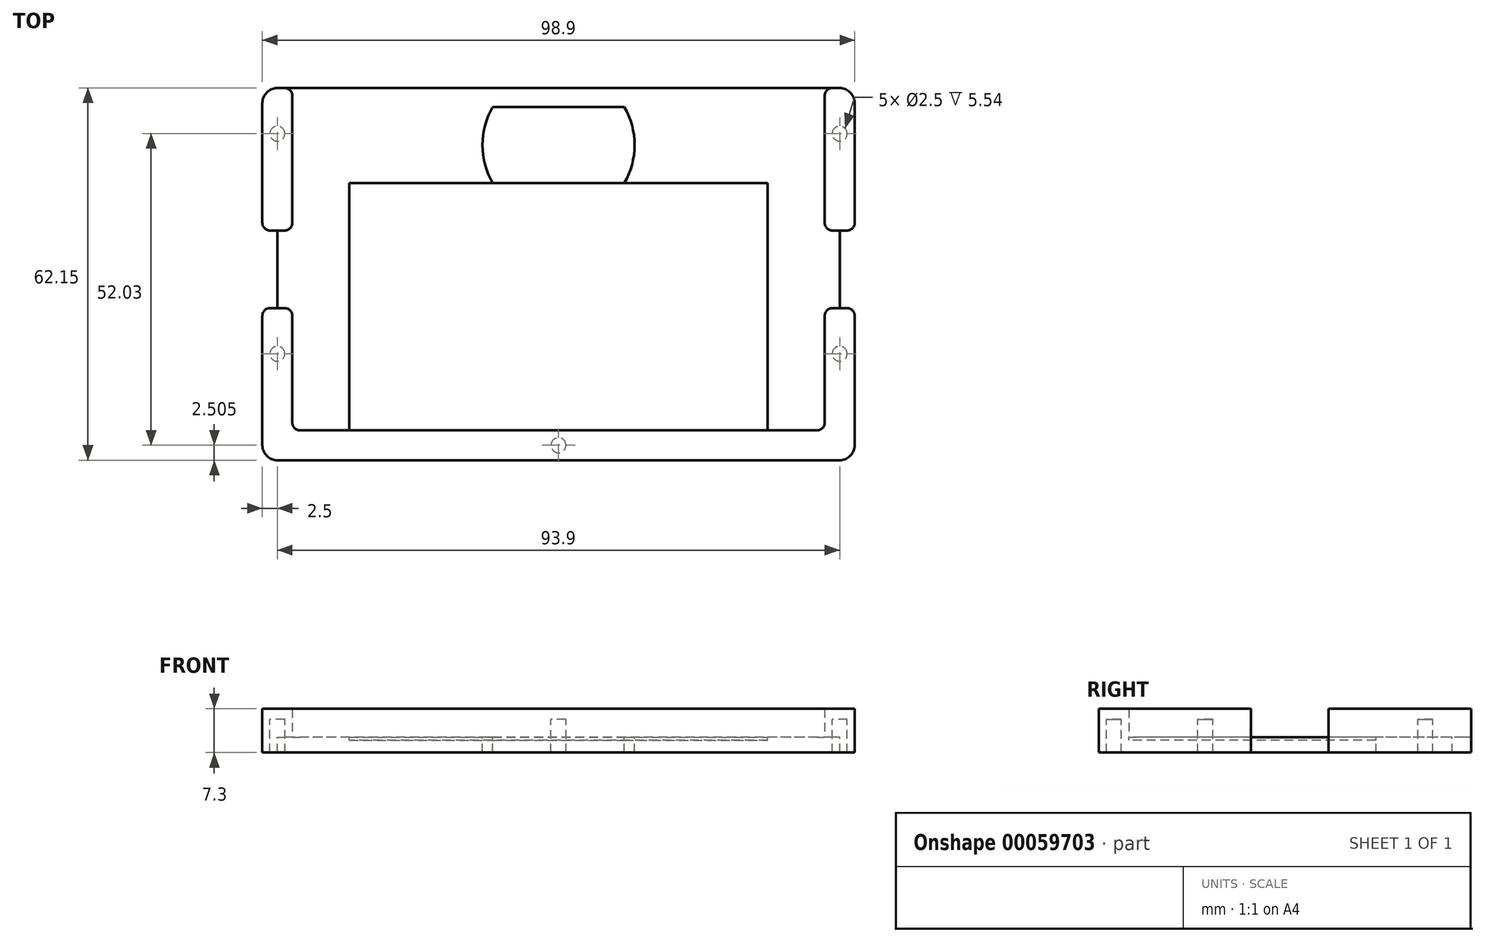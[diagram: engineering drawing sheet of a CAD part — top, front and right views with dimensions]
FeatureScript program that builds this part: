
annotation { "Feature Type Name" : "Feature", "Feature Type Description" : "" }
export const myFeature = defineFeature(function(context is Context, id is Id, definition is map)
    precondition{}
    {
        {
            var Q0;
            Q0=qCreatedBy(makeId("Top.planeOp"),FACE);
            var sketch = newSketch(context, id + "F0", { "sketchPlane" : qUnion([Q0])});
            skLineSegment(sketch, "E0.bottom", {"start": v(44.45, 28.58) * mm, "end": v(-44.45, 28.58) * mm});
            skLineSegment(sketch, "E0.top", {"start": v(44.45, -28.58) * mm, "end": v(-44.45, -28.58) * mm});
            skLineSegment(sketch, "E0.left", {"start": v(44.45, 28.58) * mm, "end": v(44.45, -28.58) * mm});
            skLineSegment(sketch, "E0.right", {"start": v(-44.45, 28.58) * mm, "end": v(-44.45, -28.58) * mm});
            skPoint(sketch, "E0.middle", {"position": v(0, 0) * mm});
            skLineSegment(sketch, "E1", {"start": v(-44.45, 28.58) * mm, "end": v(-49.45, 28.58) * mm});
            skLineSegment(sketch, "E2", {"start": v(-49.45, 28.57) * mm, "end": v(-49.45, -33.58) * mm});
            skLineSegment(sketch, "E3", {"start": v(-49.45, -33.58) * mm, "end": v(49.45, -33.57) * mm});
            skLineSegment(sketch, "E4", {"start": v(49.45, -33.57) * mm, "end": v(49.45, 28.57) * mm});
            skLineSegment(sketch, "E5", {"start": v(49.45, 28.58) * mm, "end": v(44.45, 28.58) * mm});
            skLineSegment(sketch, "E6", {"start": v(0, 0) * mm, "end": v(0, 46.56) * mm, "construction": true});
            skCircle(sketch, "E7", {"center": v(-46.95, 20.95) * mm, "radius": 1.25 * mm});
            skCircle(sketch, "E8", {"center": v(-46.95, -15.8) * mm, "radius": 1.25 * mm});
            skCircle(sketch, "E9", {"center": v(0, -31.08) * mm, "radius": 1.25 * mm});
            skCircle(sketch, "E10", {"center": v(46.95, -15.8) * mm, "radius": 1.25 * mm});
            skCircle(sketch, "E11", {"center": v(46.95, 20.95) * mm, "radius": 1.25 * mm});
            skLineSegment(sketch, "E12", {"start": v(-49.45, 4.78) * mm, "end": v(-44.45, 4.78) * mm});
            skLineSegment(sketch, "E13", {"start": v(-49.45, -8.18) * mm, "end": v(-44.45, -8.18) * mm});
            skLineSegment(sketch, "E14.MirrorCS", {"start": v(49.45, 4.78) * mm, "end": v(44.45, 4.78) * mm});
            skLineSegment(sketch, "E15.MirrorCS", {"start": v(49.45, -8.18) * mm, "end": v(44.45, -8.18) * mm});
            skLineSegment(sketch, "E16", {"start": v(-46.95, 4.78) * mm, "end": v(-46.95, -8.18) * mm});
            skLineSegment(sketch, "E17", {"start": v(46.95, 4.78) * mm, "end": v(46.95, -8.18) * mm});
            skLineSegment(sketch, "E18", {"start": v(-34.92, -28.58) * mm, "end": v(-34.93, 12.7) * mm});
            skLineSegment(sketch, "E19", {"start": v(-34.93, 12.7) * mm, "end": v(34.93, 12.7) * mm});
            skLineSegment(sketch, "E20", {"start": v(34.92, 12.7) * mm, "end": v(34.93, -28.58) * mm});
            skSolve(sketch);
        }
        {
            var Q0;
            Q0=makeQuery(id+"F0.imprint","IMPRINT",FACE,{"disambiguationData":[TD([[makeQuery(id+"F0.imprint","IMPRINT",EDGE,{"derivedFrom":sQuery(id+"F0.wireOp",EDGE,"E0.bottom")}),1.0]])]});
            var Q1;
            {var subQ1=sQuery(id+"F0.wireOp",EDGE,"E1");Q1=makeQuery(id+"F0.imprint","IMPRINT",FACE,{"disambiguationData":[TD([[makeQuery(id+"F0.imprint","IMPRINT",EDGE,{"derivedFrom":subQ1}),1.0]])]});}
            var Q2;
            {var subQ4=sQuery(id+"F0.wireOp",EDGE,"E0.top");Q2=makeQuery(id+"F0.imprint","IMPRINT",FACE,{"disambiguationData":[TD([[makeQuery(id+"F0.imprint","IMPRINT",EDGE,{"derivedFrom":subQ4}),1.0]])]});}
            var Q3;
            {var subQ5=sQuery(id+"F0.wireOp",EDGE,"E16");Q3=makeQuery(id+"F0.imprint","IMPRINT",FACE,{"disambiguationData":[TD([[makeQuery(id+"F0.imprint","IMPRINT",EDGE,{"derivedFrom":subQ5}),1.0]])]});}
            var Q4;
            {var subQ5=sQuery(id+"F0.wireOp",EDGE,"E17");Q4=makeQuery(id+"F0.imprint","IMPRINT",FACE,{"disambiguationData":[TD([[makeQuery(id+"F0.imprint","IMPRINT",EDGE,{"derivedFrom":subQ5}),-1.0]])]});}
            var Q5;
            {var subQ0=sQuery(id+"F0.wireOp",EDGE,"E5");Q5=makeQuery(id+"F0.imprint","IMPRINT",FACE,{"disambiguationData":[TD([[makeQuery(id+"F0.imprint","IMPRINT",EDGE,{"derivedFrom":subQ0}),1.0]])]});}
            var Q6;
            {var subQ0=sQuery(id+"F0.wireOp",EDGE,"E18");Q6=makeQuery(id+"F0.imprint","IMPRINT",FACE,{"disambiguationData":[TD([[makeQuery(id+"F0.imprint","IMPRINT",EDGE,{"derivedFrom":subQ0}),-1.0]])]});}
            extrude(context, id + "F1", {"entities" : qUnion([Q0, Q1, Q2, Q3, Q4, Q5, Q6]), "oppositeDirection" : true, "depth" : 2.54 * mm});
        }
        {
            var Q0;
            {var subQ1=sQuery(id+"F0.wireOp",EDGE,"E1");Q0=makeQuery(id+"F0.imprint","IMPRINT",FACE,{"disambiguationData":[TD([[makeQuery(id+"F0.imprint","IMPRINT",EDGE,{"derivedFrom":subQ1}),1.0]])]});}
            var Q1;
            {var subQ0=sQuery(id+"F0.wireOp",EDGE,"E5");Q1=makeQuery(id+"F0.imprint","IMPRINT",FACE,{"disambiguationData":[TD([[makeQuery(id+"F0.imprint","IMPRINT",EDGE,{"derivedFrom":subQ0}),1.0]])]});}
            var Q2;
            Q2=makeQuery(id+"F0.imprint","IMPRINT",FACE,{"disambiguationData":[TD([[makeQuery(id+"F0.imprint","IMPRINT",EDGE,{"derivedFrom":sQuery(id+"F0.wireOp",EDGE,"E8")}),1.0]])]});
            var Q3;
            Q3=makeQuery(id+"F0.imprint","IMPRINT",FACE,{"disambiguationData":[TD([[makeQuery(id+"F0.imprint","IMPRINT",EDGE,{"derivedFrom":sQuery(id+"F0.wireOp",EDGE,"E7")}),1.0]])]});
            var Q4;
            Q4=makeQuery(id+"F0.imprint","IMPRINT",FACE,{"disambiguationData":[TD([[makeQuery(id+"F0.imprint","IMPRINT",EDGE,{"derivedFrom":sQuery(id+"F0.wireOp",EDGE,"E11")}),1.0]])]});
            var Q5;
            {var subQ4=sQuery(id+"F0.wireOp",EDGE,"E0.top");Q5=makeQuery(id+"F0.imprint","IMPRINT",FACE,{"disambiguationData":[TD([[makeQuery(id+"F0.imprint","IMPRINT",EDGE,{"derivedFrom":subQ4}),1.0]])]});}
            var Q6;
            Q6=makeQuery(id+"F0.imprint","IMPRINT",FACE,{"disambiguationData":[TD([[makeQuery(id+"F0.imprint","IMPRINT",EDGE,{"derivedFrom":sQuery(id+"F0.wireOp",EDGE,"E9")}),1.0]])]});
            var Q7;
            Q7=makeQuery(id+"F0.imprint","IMPRINT",FACE,{"disambiguationData":[TD([[makeQuery(id+"F0.imprint","IMPRINT",EDGE,{"derivedFrom":sQuery(id+"F0.wireOp",EDGE,"E10")}),1.0]])]});
            extrude(context, id + "F2", {"entities" : qUnion([Q0, Q1, Q2, Q3, Q4, Q5, Q6, Q7]), "depth" : 4.76 * mm});
        }
        {
            var Q0;
            {var subQ0=sQuery(id+"F0.wireOp",EDGE,"E18");Q0=makeQuery(id+"F0.imprint","IMPRINT",FACE,{"disambiguationData":[TD([[makeQuery(id+"F0.imprint","IMPRINT",EDGE,{"derivedFrom":subQ0}),-1.0]])]});}
            var Q1;
            {var subQ1=sQuery(id+"F0.wireOp",EDGE,"E3");Q1=makeQuery(id+"F0.imprint","IMPRINT",FACE,{"disambiguationData":[TD([[makeQuery(id+"F0.imprint","IMPRINT",EDGE,{"derivedFrom":subQ1}),1.0]])]});}
            var Q2;
            {var subQ0=sQuery(id+"F0.wireOp",EDGE,"E5");Q2=makeQuery(id+"F0.imprint","IMPRINT",FACE,{"disambiguationData":[TD([[makeQuery(id+"F0.imprint","IMPRINT",EDGE,{"derivedFrom":subQ0}),1.0]])]});}
            var Q3;
            {var subQ1=sQuery(id+"F0.wireOp",EDGE,"E1");Q3=makeQuery(id+"F0.imprint","IMPRINT",FACE,{"disambiguationData":[TD([[makeQuery(id+"F0.imprint","IMPRINT",EDGE,{"derivedFrom":subQ1}),1.0]])]});}
            extrude(context, id + "F3", {"entities" : qUnion([Q0, Q1, Q2, Q3]), "operationType" : NewBodyOperationType.REMOVE, "oppositeDirection" : true, "depth" : 0.5 * mm});
        }
        {
            var Q0;
            Q0=makeQuery(id+"F2.opExtrude","CAP_FACE",FACE,{"disambiguationData":[OSD([sQuery(id+"F0.wireOp",EDGE,"E0.top"),sQuery(id+"F0.wireOp",EDGE,"E0.left"),sQuery(id+"F0.wireOp",EDGE,"E0.right"),sQuery(id+"F0.wireOp",EDGE,"E2"),sQuery(id+"F0.wireOp",EDGE,"E3"),sQuery(id+"F0.wireOp",EDGE,"E4"),sQuery(id+"F0.wireOp",EDGE,"E13"),sQuery(id+"F0.wireOp",EDGE,"E15.MirrorCS")])],"isStart":true});
            var Q1;
            Q1=makeQuery(id+"F2.opExtrude","CAP_FACE",FACE,{"disambiguationData":[OSD([sQuery(id+"F0.wireOp",EDGE,"E0.left"),sQuery(id+"F0.wireOp",EDGE,"E4"),sQuery(id+"F0.wireOp",EDGE,"E5"),sQuery(id+"F0.wireOp",EDGE,"E14.MirrorCS")])],"isStart":true});
            var Q2;
            Q2=makeQuery(id+"F2.opExtrude","CAP_FACE",FACE,{"disambiguationData":[OSD([sQuery(id+"F0.wireOp",EDGE,"E0.right"),sQuery(id+"F0.wireOp",EDGE,"E1"),sQuery(id+"F0.wireOp",EDGE,"E2"),sQuery(id+"F0.wireOp",EDGE,"E12")])],"isStart":true});
            extrude(context, id + "F4", {"entities" : qUnion([Q0, Q1, Q2]), "operationType" : NewBodyOperationType.ADD, "depth" : 0.5 * mm});
        }
        {
            var Q0;
            Q0=makeQuery(id+"F0.imprint","IMPRINT",FACE,{"disambiguationData":[TD([[makeQuery(id+"F0.imprint","IMPRINT",EDGE,{"derivedFrom":sQuery(id+"F0.wireOp",EDGE,"E8")}),1.0]])]});
            var Q1;
            Q1=makeQuery(id+"F0.imprint","IMPRINT",FACE,{"disambiguationData":[TD([[makeQuery(id+"F0.imprint","IMPRINT",EDGE,{"derivedFrom":sQuery(id+"F0.wireOp",EDGE,"E9")}),1.0]])]});
            var Q2;
            Q2=makeQuery(id+"F0.imprint","IMPRINT",FACE,{"disambiguationData":[TD([[makeQuery(id+"F0.imprint","IMPRINT",EDGE,{"derivedFrom":sQuery(id+"F0.wireOp",EDGE,"E10")}),1.0]])]});
            var Q3;
            Q3=makeQuery(id+"F0.imprint","IMPRINT",FACE,{"disambiguationData":[TD([[makeQuery(id+"F0.imprint","IMPRINT",EDGE,{"derivedFrom":sQuery(id+"F0.wireOp",EDGE,"E11")}),1.0]])]});
            var Q4;
            Q4=makeQuery(id+"F0.imprint","IMPRINT",FACE,{"disambiguationData":[TD([[makeQuery(id+"F0.imprint","IMPRINT",EDGE,{"derivedFrom":sQuery(id+"F0.wireOp",EDGE,"E7")}),1.0]])]});
            extrude(context, id + "F5", {"entities" : qUnion([Q0, Q1, Q2, Q3, Q4]), "operationType" : NewBodyOperationType.REMOVE, "endBound" : BoundingType.SYMMETRIC, "depth" : 6 * mm});
        }
        {
            var Q0;
            Q0=makeQuery(id+"F2.opExtrude","SWEPT_EDGE",EDGE,{"disambiguationData":[OSD([sQuery(id+"F0.wireOp",EDGE,"E2"),sQuery(id+"F0.wireOp",EDGE,"E3")])]});
            var Q1;
            Q1=makeQuery(id+"F1.opExtrude","SWEPT_EDGE",EDGE,{"disambiguationData":[OSD([sQuery(id+"F0.wireOp",EDGE,"E2"),sQuery(id+"F0.wireOp",EDGE,"E3")])]});
            var Q2;
            Q2=makeQuery(id+"F1.opExtrude","SWEPT_EDGE",EDGE,{"disambiguationData":[OSD([sQuery(id+"F0.wireOp",EDGE,"E1"),sQuery(id+"F0.wireOp",EDGE,"E2")])]});
            var Q3;
            Q3=makeQuery(id+"F2.opExtrude","SWEPT_EDGE",EDGE,{"disambiguationData":[OSD([sQuery(id+"F0.wireOp",EDGE,"E1"),sQuery(id+"F0.wireOp",EDGE,"E2")])]});
            var Q4;
            Q4=makeQuery(id+"F1.opExtrude","SWEPT_EDGE",EDGE,{"disambiguationData":[OSD([sQuery(id+"F0.wireOp",EDGE,"E3"),sQuery(id+"F0.wireOp",EDGE,"E4")])]});
            var Q5;
            Q5=makeQuery(id+"F2.opExtrude","SWEPT_EDGE",EDGE,{"disambiguationData":[OSD([sQuery(id+"F0.wireOp",EDGE,"E3"),sQuery(id+"F0.wireOp",EDGE,"E4")])]});
            var Q6;
            Q6=makeQuery(id+"F2.opExtrude","SWEPT_EDGE",EDGE,{"disambiguationData":[OSD([sQuery(id+"F0.wireOp",EDGE,"E4"),sQuery(id+"F0.wireOp",EDGE,"E5")])]});
            var Q7;
            Q7=makeQuery(id+"F1.opExtrude","SWEPT_EDGE",EDGE,{"disambiguationData":[OSD([sQuery(id+"F0.wireOp",EDGE,"E4"),sQuery(id+"F0.wireOp",EDGE,"E5")])]});
            fillet(context, id + "F6", {"entities" : qUnion([Q0, Q1, Q2, Q3, Q4, Q5, Q6, Q7]), "radius" : 2.54 * mm, "tangentPropagation" : true, "allowEdgeOverflow" : false});
        }
        {
            var Q0;
            Q0=makeQuery(id+"F1.opExtrude","SWEPT_EDGE",EDGE,{"disambiguationData":[OSD([sQuery(id+"F0.wireOp",EDGE,"E4"),sQuery(id+"F0.wireOp",EDGE,"E14.MirrorCS")])]});
            var Q1;
            Q1=makeQuery(id+"F2.opExtrude","SWEPT_EDGE",EDGE,{"disambiguationData":[OSD([sQuery(id+"F0.wireOp",EDGE,"E4"),sQuery(id+"F0.wireOp",EDGE,"E14.MirrorCS")])]});
            var Q2;
            Q2=makeQuery(id+"F1.opExtrude","SWEPT_EDGE",EDGE,{"disambiguationData":[OSD([sQuery(id+"F0.wireOp",EDGE,"E4"),sQuery(id+"F0.wireOp",EDGE,"E15.MirrorCS")])]});
            var Q3;
            Q3=makeQuery(id+"F2.opExtrude","SWEPT_EDGE",EDGE,{"disambiguationData":[OSD([sQuery(id+"F0.wireOp",EDGE,"E4"),sQuery(id+"F0.wireOp",EDGE,"E15.MirrorCS")])]});
            var Q4;
            Q4=makeQuery(id+"F1.opExtrude","SWEPT_EDGE",EDGE,{"disambiguationData":[OSD([sQuery(id+"F0.wireOp",EDGE,"E2"),sQuery(id+"F0.wireOp",EDGE,"E12")])]});
            var Q5;
            Q5=makeQuery(id+"F2.opExtrude","SWEPT_EDGE",EDGE,{"disambiguationData":[OSD([sQuery(id+"F0.wireOp",EDGE,"E2"),sQuery(id+"F0.wireOp",EDGE,"E12")])]});
            var Q6;
            Q6=makeQuery(id+"F2.opExtrude","SWEPT_EDGE",EDGE,{"disambiguationData":[OSD([sQuery(id+"F0.wireOp",EDGE,"E2"),sQuery(id+"F0.wireOp",EDGE,"E13")])]});
            var Q7;
            Q7=makeQuery(id+"F1.opExtrude","SWEPT_EDGE",EDGE,{"disambiguationData":[OSD([sQuery(id+"F0.wireOp",EDGE,"E2"),sQuery(id+"F0.wireOp",EDGE,"E13")])]});
            var Q8;
            Q8=makeQuery(id+"F2.opExtrude","SWEPT_EDGE",EDGE,{"disambiguationData":[OSD([sQuery(id+"F0.wireOp",EDGE,"E0.right"),sQuery(id+"F0.wireOp",EDGE,"E12")])]});
            var Q9;
            Q9=makeQuery(id+"F2.opExtrude","SWEPT_EDGE",EDGE,{"disambiguationData":[OSD([sQuery(id+"F0.wireOp",EDGE,"E0.right"),sQuery(id+"F0.wireOp",EDGE,"E13")])]});
            var Q10;
            Q10=makeQuery(id+"F2.opExtrude","SWEPT_EDGE",EDGE,{"disambiguationData":[OSD([sQuery(id+"F0.wireOp",EDGE,"E0.left"),sQuery(id+"F0.wireOp",EDGE,"E15.MirrorCS")])]});
            var Q11;
            Q11=makeQuery(id+"F2.opExtrude","SWEPT_EDGE",EDGE,{"disambiguationData":[OSD([sQuery(id+"F0.wireOp",EDGE,"E0.left"),sQuery(id+"F0.wireOp",EDGE,"E14.MirrorCS")])]});
            var Q12;
            Q12=makeQuery(id+"F2.opExtrude","SWEPT_EDGE",EDGE,{"disambiguationData":[OSD([sQuery(id+"F0.wireOp",EDGE,"E0.bottom"),sQuery(id+"F0.wireOp",EDGE,"E0.left"),sQuery(id+"F0.wireOp",EDGE,"E5")])]});
            var Q13;
            Q13=makeQuery(id+"F2.opExtrude","SWEPT_EDGE",EDGE,{"disambiguationData":[OSD([sQuery(id+"F0.wireOp",EDGE,"E0.bottom"),sQuery(id+"F0.wireOp",EDGE,"E0.right"),sQuery(id+"F0.wireOp",EDGE,"E1")])]});
            var Q14;
            Q14=makeQuery(id+"F2.opExtrude","SWEPT_EDGE",EDGE,{"disambiguationData":[OSD([sQuery(id+"F0.wireOp",EDGE,"E0.top"),sQuery(id+"F0.wireOp",EDGE,"E0.right")])]});
            var Q15;
            Q15=makeQuery(id+"F2.opExtrude","SWEPT_EDGE",EDGE,{"disambiguationData":[OSD([sQuery(id+"F0.wireOp",EDGE,"E0.top"),sQuery(id+"F0.wireOp",EDGE,"E0.left")])]});
            var Q16;
            Q16=makeQuery(id+"F3.boolean.opBoolean","COPY",EDGE,{"derivedFrom":makeQuery(id+"F3.opExtrude","SWEPT_EDGE",EDGE,{"disambiguationData":[OSD([sQuery(id+"F0.wireOp",EDGE,"E0.top"),sQuery(id+"F0.wireOp",EDGE,"E0.left")])]})});
            var Q17;
            Q17=makeQuery(id+"F3.boolean.opBoolean","COPY",EDGE,{"derivedFrom":makeQuery(id+"F3.opExtrude","SWEPT_EDGE",EDGE,{"disambiguationData":[OSD([sQuery(id+"F0.wireOp",EDGE,"E0.top"),sQuery(id+"F0.wireOp",EDGE,"E0.right")])]})});
            fillet(context, id + "F7", {"entities" : qUnion([Q0, Q1, Q2, Q3, Q4, Q5, Q6, Q7, Q8, Q9, Q10, Q11, Q12, Q13, Q14, Q15, Q16, Q17]), "radius" : 1.27 * mm, "tangentPropagation" : true, "allowEdgeOverflow" : false});
        }
        {
            var Q0;
            Q0=makeQuery(id+"F1.opExtrude","CAP_FACE",FACE,{"disambiguationData":[OSD([sQuery(id+"F0.wireOp",EDGE,"E0.bottom"),sQuery(id+"F0.wireOp",EDGE,"E1"),sQuery(id+"F0.wireOp",EDGE,"E2"),sQuery(id+"F0.wireOp",EDGE,"E3"),sQuery(id+"F0.wireOp",EDGE,"E4"),sQuery(id+"F0.wireOp",EDGE,"E5"),sQuery(id+"F0.wireOp",EDGE,"E7"),sQuery(id+"F0.wireOp",EDGE,"E8"),sQuery(id+"F0.wireOp",EDGE,"E9"),sQuery(id+"F0.wireOp",EDGE,"E10"),sQuery(id+"F0.wireOp",EDGE,"E11"),sQuery(id+"F0.wireOp",EDGE,"E12"),sQuery(id+"F0.wireOp",EDGE,"E13"),sQuery(id+"F0.wireOp",EDGE,"E14.MirrorCS"),sQuery(id+"F0.wireOp",EDGE,"E15.MirrorCS"),sQuery(id+"F0.wireOp",EDGE,"E16"),sQuery(id+"F0.wireOp",EDGE,"E17")])],"isStart":true});
            var sketch = newSketch(context, id + "F8", { "sketchPlane" : qUnion([Q0])});
            skLineSegment(sketch, "E21", {"start": v(0, 0) * mm, "end": v(0, 56.1) * mm, "construction": true});
            skCircle(sketch, "E22", {"center": v(0, 19.05) * mm, "radius": 12.7 * mm});
            skPoint(sketch, "E23", {"position": v(0, 12.7) * mm});
            skLineSegment(sketch, "E24", {"start": v(-11, 25.4) * mm, "end": v(11, 25.4) * mm});
            skLineSegment(sketch, "E25", {"start": v(0, 19.05) * mm, "end": v(12.7, 19.05) * mm, "construction": true});
            skLineSegment(sketch, "E26", {"start": v(-11, 12.7) * mm, "end": v(11, 12.7) * mm});
            skSolve(sketch);
        }
        {
            var Q0;
            {var subQ0=sQuery(id+"F8.wireOp",EDGE,"E24");Q0=makeQuery(id+"F8.imprint","IMPRINT",FACE,{"disambiguationData":[TD([[makeQuery(id+"F8.imprint","IMPRINT",EDGE,{"derivedFrom":subQ0}),-1.0]])]});}
            extrude(context, id + "F9", {"entities" : qUnion([Q0]), "operationType" : NewBodyOperationType.REMOVE, "endBound" : BoundingType.THROUGH_ALL, "oppositeDirection" : true, "depth" : 25.4 * mm});
        }
    });
